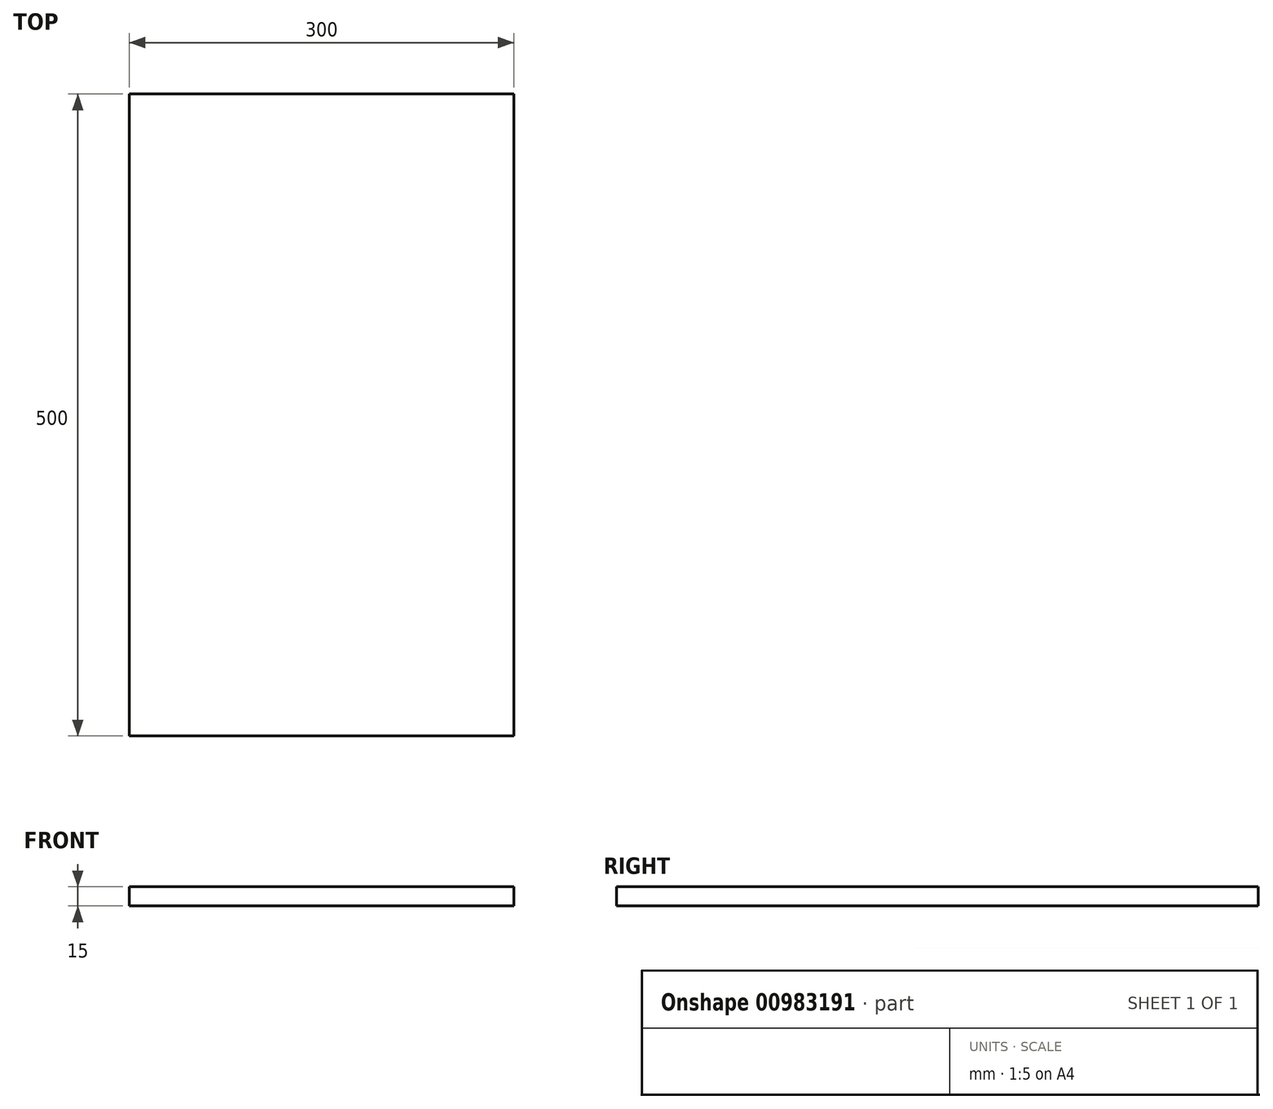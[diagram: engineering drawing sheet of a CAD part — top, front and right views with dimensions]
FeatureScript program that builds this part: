
annotation { "Feature Type Name" : "Feature", "Feature Type Description" : "" }
export const myFeature = defineFeature(function(context is Context, id is Id, definition is map)
    precondition{}
    {
        {
            var Q0;
            Q0=qCreatedBy(makeId("Top.planeOp"),FACE);
            var sketch = newSketch(context, id + "F0", { "sketchPlane" : qUnion([Q0])});
            skLineSegment(sketch, "E0.bottom", {"start": v(150, -250) * mm, "end": v(-150, -250) * mm});
            skLineSegment(sketch, "E0.top", {"start": v(150, 250) * mm, "end": v(-150, 250) * mm});
            skLineSegment(sketch, "E0.left", {"start": v(150, -250) * mm, "end": v(150, 250) * mm});
            skLineSegment(sketch, "E0.right", {"start": v(-150, -250) * mm, "end": v(-150, 250) * mm});
            skPoint(sketch, "E0.middle", {"position": v(0, 0) * mm});
            skSolve(sketch);
        }
        {
            var Q0;
            Q0=makeQuery(id+"F0.imprint","IMPRINT",FACE,{"disambiguationData":[TD([[makeQuery(id+"F0.imprint","IMPRINT",EDGE,{"derivedFrom":sQuery(id+"F0.wireOp",EDGE,"E0.bottom")}),-1.0]])]});
            extrude(context, id + "F1", {"entities" : qUnion([Q0]), "depth" : 15 * mm, "offsetDistance" : 25 * mm});
        }
    });
